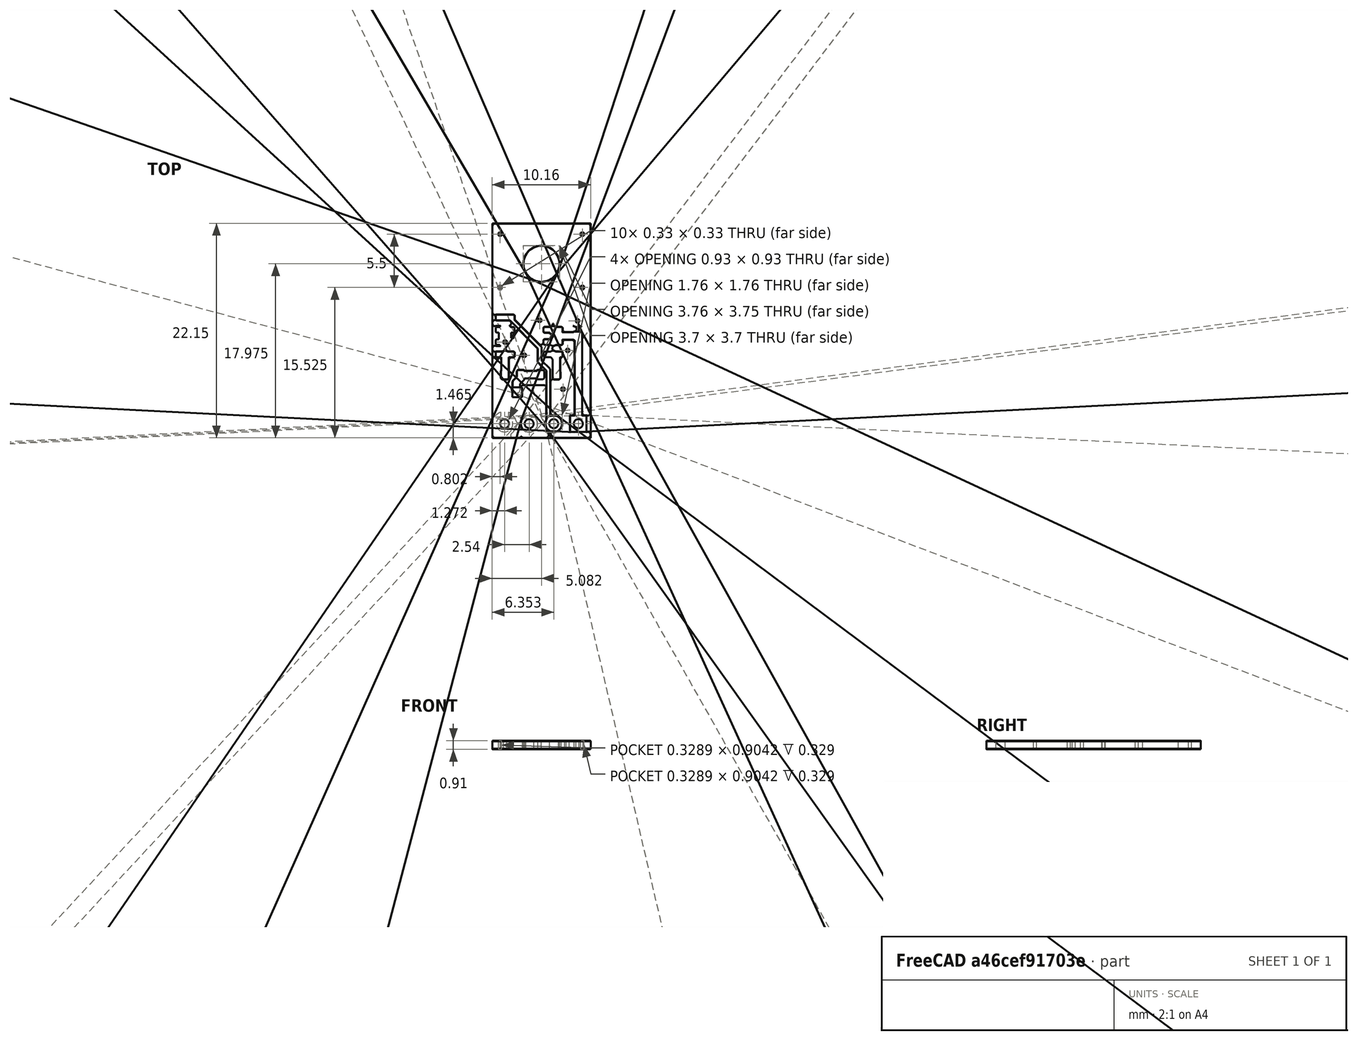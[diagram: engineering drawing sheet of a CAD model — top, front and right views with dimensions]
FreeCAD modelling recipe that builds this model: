
FCSTD DOCUMENT  (FreeCAD 0.21R29506 (Git))
Label: heat_sim
License: All rights reserved
LicenseURL: http://en.wikipedia.org/wiki/All_rights_reserved
objects: Path::FeatureArea×35, Part::Feature×33, Part::Extrusion×5, Part::Compound×4, Part::MultiFuse×2, App::MaterialObjectPython×2, Fem::ConstraintTemperature×2, Part::Cut×1, Part::Box×1, Fem::FemMeshObjectPython×1, App::FeaturePython×1, App::TextDocument×1, Fem::FemPostPipeline×1, Fem::FemSolverObjectPython×1, Fem::FemAnalysis×1
note: 116 computed .brp shape members not serialized (recipe doc carries the construction recipe); baked Part::Feature solids carry a one-line shape summary decoded from their .brp

FEATURE [Part::Feature] holes_wire  label="holes_wire#F.Cu#0"
  shape: bbox 3.7 x 3.7 x 2e-07 mm, 0 faces, 0 solids (baked)
FEATURE [Part::Feature] pads_wire  label="pads_wire#F.Cu#0#"REF**""
  shape: bbox 3.7 x 3.7 x 2e-07 mm, 0 faces, 0 solids (baked)
FEATURE [Path::FeatureArea] pads_area  label="pads_area#F.Cu#0#"REF**""
  Accuracy = 0.0005
  Angle = 45
  AngleShift = 0
  CleanDistance = 0
  ClipFill = 0
  ClipperScale = 10000000
  Coplanar = 0
  Deflection = 0.01
  EndType = 0
  Explode = false
  ExtraPass = 0
  Fill = 1
  FitArcs = false
  FromCenter = false
  JoinType = 0
  LastStepover = 0
  MaxArcPoints = 100
  MinArcPoints = 4
  MiterLimit = 2
  OpenMode = 0
  Operation = 0
  Outline = false
  Placement = pos=(4.90232,-4.455,0) rot=(0,0,1;0rad)
  PocketExtraOffset = 0
  PocketLastStepover = 0
  PocketMode = 0
  PocketStepover = 0
  Project = false
  Reorient = false
  RoundPrecision = 0
  SectionCount = 0
  SectionMode = 2
  SectionOffset = 0
  SectionTolerance = 1e-06
  Shift = 0
  Simplify = false
  Sources = -> [pads_wire]
  Stepdown = 1
  Stepover = 0
  SubjectFill = 0
  Thicken = false
  Tolerance = 1e-07
  ToolRadius = 1
  Unit = 1
FEATURE [Part::Feature] pads_wire001  label="pads_wire001#F.Cu#1#"Q1""
  shape: bbox 0.65 x 0.65 x 2e-07 mm, 0 faces, 0 solids (baked)
FEATURE [Path::FeatureArea] pads_area001  label="pads_area001#F.Cu#1#"Q1""
  Accuracy = 0.0005
  Angle = 45
  AngleShift = 0
  CleanDistance = 0
  ClipFill = 0
  ClipperScale = 10000000
  Coplanar = 0
  Deflection = 0.01
  EndType = 0
  Explode = false
  ExtraPass = 0
  Fill = 1
  FitArcs = false
  FromCenter = false
  JoinType = 0
  LastStepover = 0
  MaxArcPoints = 100
  MinArcPoints = 4
  MiterLimit = 2
  OpenMode = 0
  Operation = 0
  Outline = false
  Placement = pos=(2.34232,-18.285,0) rot=(0,0,1;1.5708rad)
  PocketExtraOffset = 0
  PocketLastStepover = 0
  PocketMode = 0
  PocketStepover = 0
  Project = false
  Reorient = false
  RoundPrecision = 0
  SectionCount = 0
  SectionMode = 2
  SectionOffset = 0
  SectionTolerance = 1e-06
  Shift = 0
  Simplify = false
  Sources = -> [pads_wire001]
  Stepdown = 1
  Stepover = 0
  SubjectFill = 0
  Thicken = false
  Tolerance = 1e-07
  ToolRadius = 1
  Unit = 1
FEATURE [Part::Feature] pads_wire002  label="pads_wire002#F.Cu#2#"C1""
  shape: bbox 2.45 x 0.95 x 2e-07 mm, 0 faces, 0 solids (baked)
FEATURE [Path::FeatureArea] pads_area002  label="pads_area002#F.Cu#2#"C1""
  Accuracy = 0.0005
  Angle = 45
  AngleShift = 0
  CleanDistance = 0
  ClipFill = 0
  ClipperScale = 10000000
  Coplanar = 0
  Deflection = 0.01
  EndType = 0
  Explode = false
  ExtraPass = 0
  Fill = 1
  FitArcs = false
  FromCenter = false
  JoinType = 0
  LastStepover = 0
  MaxArcPoints = 100
  MinArcPoints = 4
  MiterLimit = 2
  OpenMode = 0
  Operation = 0
  Outline = false
  Placement = pos=(8.62232,-11.13,0) rot=(0,0,1;1.5708rad)
  PocketExtraOffset = 0
  PocketLastStepover = 0
  PocketMode = 0
  PocketStepover = 0
  Project = false
  Reorient = false
  RoundPrecision = 0
  SectionCount = 0
  SectionMode = 2
  SectionOffset = 0
  SectionTolerance = 1e-06
  Shift = 0
  Simplify = false
  Sources = -> [pads_wire002]
  Stepdown = 1
  Stepover = 0
  SubjectFill = 0
  Thicken = false
  Tolerance = 1e-07
  ToolRadius = 1
  Unit = 1
FEATURE [Part::Feature] pads_wire003  label="pads_wire003#F.Cu#3#"R2""
  shape: bbox 2.45 x 0.95 x 2e-07 mm, 0 faces, 0 solids (baked)
FEATURE [Path::FeatureArea] pads_area003  label="pads_area003#F.Cu#3#"R2""
  Accuracy = 0.0005
  Angle = 45
  AngleShift = 0
  CleanDistance = 0
  ClipFill = 0
  ClipperScale = 10000000
  Coplanar = 0
  Deflection = 0.01
  EndType = 0
  Explode = false
  ExtraPass = 0
  Fill = 1
  FitArcs = false
  FromCenter = false
  JoinType = 0
  LastStepover = 0
  MaxArcPoints = 100
  MinArcPoints = 4
  MiterLimit = 2
  OpenMode = 0
  Operation = 0
  Outline = false
  Placement = pos=(5.62232,-15.905,0) rot=(0,0,1;3.14159rad)
  PocketExtraOffset = 0
  PocketLastStepover = 0
  PocketMode = 0
  PocketStepover = 0
  Project = false
  Reorient = false
  RoundPrecision = 0
  SectionCount = 0
  SectionMode = 2
  SectionOffset = 0
  SectionTolerance = 1e-06
  Shift = 0
  Simplify = false
  Sources = -> [pads_wire003]
  Stepdown = 1
  Stepover = 0
  SubjectFill = 0
  Thicken = false
  Tolerance = 1e-07
  ToolRadius = 1
  Unit = 1
FEATURE [Part::Feature] pads_wire004  label="pads_wire004#F.Cu#4#"R1""
  shape: bbox 2.45 x 0.95 x 2e-07 mm, 0 faces, 0 solids (baked)
FEATURE [Path::FeatureArea] pads_area004  label="pads_area004#F.Cu#4#"R1""
  Accuracy = 0.0005
  Angle = 45
  AngleShift = 0
  CleanDistance = 0
  ClipFill = 0
  ClipperScale = 10000000
  Coplanar = 0
  Deflection = 0.01
  EndType = 0
  Explode = false
  ExtraPass = 0
  Fill = 1
  FitArcs = false
  FromCenter = false
  JoinType = 0
  LastStepover = 0
  MaxArcPoints = 100
  MinArcPoints = 4
  MiterLimit = 2
  OpenMode = 0
  Operation = 0
  Outline = false
  Placement = pos=(1.94732,-15.905,0) rot=(0,0,1;0rad)
  PocketExtraOffset = 0
  PocketLastStepover = 0
  PocketMode = 0
  PocketStepover = 0
  Project = false
  Reorient = false
  RoundPrecision = 0
  SectionCount = 0
  SectionMode = 2
  SectionOffset = 0
  SectionTolerance = 1e-06
  Shift = 0
  Simplify = false
  Sources = -> [pads_wire004]
  Stepdown = 1
  Stepover = 0
  SubjectFill = 0
  Thicken = false
  Tolerance = 1e-07
  ToolRadius = 1
  Unit = 1
FEATURE [Part::Feature] pads_wire005  label="pads_wire005#F.Cu#5#"U1""
  shape: bbox 6.9 x 4.41 x 2e-07 mm, 0 faces, 0 solids (baked)
FEATURE [Path::FeatureArea] pads_area005  label="pads_area005#F.Cu#5#"U1""
  Accuracy = 0.0005
  Angle = 45
  AngleShift = 0
  CleanDistance = 0
  ClipFill = 0
  ClipperScale = 10000000
  Coplanar = 0
  Deflection = 0.01
  EndType = 0
  Explode = false
  ExtraPass = 0
  Fill = 1
  FitArcs = false
  FromCenter = false
  JoinType = 0
  LastStepover = 0
  MaxArcPoints = 100
  MinArcPoints = 4
  MiterLimit = 2
  OpenMode = 0
  Operation = 0
  Outline = false
  Placement = pos=(3.62232,-11.905,0) rot=(0,0,1;0rad)
  PocketExtraOffset = 0
  PocketLastStepover = 0
  PocketMode = 0
  PocketStepover = 0
  Project = false
  Reorient = false
  RoundPrecision = 0
  SectionCount = 0
  SectionMode = 2
  SectionOffset = 0
  SectionTolerance = 1e-06
  Shift = 0
  Simplify = false
  Sources = -> [pads_wire005]
  Stepdown = 1
  Stepover = 0
  SubjectFill = 0
  Thicken = false
  Tolerance = 1e-07
  ToolRadius = 1
  Unit = 1
FEATURE [Part::Feature] pads_wire006  label="pads_wire006#F.Cu#6#"J1""
  shape: bbox 1.7 x 9.32 x 2e-07 mm, 0 faces, 0 solids (baked)
FEATURE [Path::FeatureArea] pads_area006  label="pads_area006#F.Cu#6#"J1""
  Accuracy = 0.0005
  Angle = 45
  AngleShift = 0
  CleanDistance = 0
  ClipFill = 0
  ClipperScale = 10000000
  Coplanar = 0
  Deflection = 0.01
  EndType = 0
  Explode = false
  ExtraPass = 0
  Fill = 1
  FitArcs = false
  FromCenter = false
  JoinType = 0
  LastStepover = 0
  MaxArcPoints = 100
  MinArcPoints = 4
  MiterLimit = 2
  OpenMode = 0
  Operation = 0
  Outline = false
  Placement = pos=(8.71232,-20.965,0) rot=(0,0,-1;1.5708rad)
  PocketExtraOffset = 0
  PocketLastStepover = 0
  PocketMode = 0
  PocketStepover = 0
  Project = false
  Reorient = false
  RoundPrecision = 0
  SectionCount = 0
  SectionMode = 2
  SectionOffset = 0
  SectionTolerance = 1e-06
  Shift = 0
  Simplify = false
  Sources = -> [pads_wire006]
  Stepdown = 1
  Stepover = 0
  SubjectFill = 0
  Thicken = false
  Tolerance = 1e-07
  ToolRadius = 1
  Unit = 1
FEATURE [Part::Feature] vias_wire  label="vias_wire#F.Cu"
  shape: bbox 9.3 x 16.8 x 2e-07 mm, 0 faces, 0 solids (baked)
FEATURE [Path::FeatureArea] vias_area  label="vias_area#F.Cu"
  Accuracy = 0.0005
  Angle = 45
  AngleShift = 0
  CleanDistance = 0
  ClipFill = 0
  ClipperScale = 10000000
  Coplanar = 0
  Deflection = 0.01
  EndType = 0
  Explode = false
  ExtraPass = 0
  Fill = 1
  FitArcs = false
  FromCenter = false
  JoinType = 0
  LastStepover = 0
  MaxArcPoints = 100
  MinArcPoints = 4
  MiterLimit = 2
  OpenMode = 0
  Operation = 0
  Outline = false
  PocketExtraOffset = 0
  PocketLastStepover = 0
  PocketMode = 0
  PocketStepover = 0
  Project = false
  Reorient = false
  RoundPrecision = 0
  SectionCount = 0
  SectionMode = 2
  SectionOffset = 0
  SectionTolerance = 1e-06
  Shift = 0
  Simplify = false
  Sources = -> [vias_wire]
  Stepdown = 1
  Stepover = 0
  SubjectFill = 0
  Thicken = false
  Tolerance = 1e-07
  ToolRadius = 1
  Unit = 1
FEATURE [Part::Compound] pads_combo  label="pads_combo#F.Cu"
  Links = -> [pads_area,pads_area001,pads_area002,pads_area003,pads_area004,pads_area005,pads_area006,vias_area]
FEATURE [Path::FeatureArea] pads_area007  label="pads_area007#F.Cu"
  Accuracy = 0.0005
  Angle = 45
  AngleShift = 0
  CleanDistance = 0
  ClipFill = 0
  ClipperScale = 10000000
  Coplanar = 0
  Deflection = 0.01
  EndType = 0
  Explode = false
  ExtraPass = 0
  Fill = 2
  FitArcs = true
  FromCenter = false
  JoinType = 0
  LastStepover = 0
  MaxArcPoints = 100
  MinArcPoints = 4
  MiterLimit = 2
  OpenMode = 0
  Operation = 1
  Outline = false
  PocketExtraOffset = 0
  PocketLastStepover = 0
  PocketMode = 0
  PocketStepover = 0
  Project = false
  Reorient = false
  RoundPrecision = 0
  SectionCount = 0
  SectionMode = 2
  SectionOffset = 0
  SectionTolerance = 1e-06
  Shift = 0
  Simplify = false
  Sources = -> [pads_combo,holes_wire]
  Stepdown = 1
  Stepover = 0
  SubjectFill = 0
  Thicken = false
  Tolerance = 1e-07
  ToolRadius = 1
  Unit = 1
FEATURE [Part::Feature] track_wire  label="track_wire#F.Cu#0.762"
  shape: bbox 7.59 x 9.695 x 2e-07 mm, 0 faces, 0 solids (baked)
FEATURE [Path::FeatureArea] track_area  label="track_area#F.Cu#0.762"
  Accuracy = 0.0005
  Angle = 45
  AngleShift = 0
  CleanDistance = 0
  ClipFill = 0
  ClipperScale = 10000000
  Coplanar = 0
  Deflection = 0.01
  EndType = 0
  Explode = false
  ExtraPass = 0
  Fill = 1
  FitArcs = true
  FromCenter = false
  JoinType = 0
  LastStepover = 0
  MaxArcPoints = 100
  MinArcPoints = 4
  MiterLimit = 2
  Offset = 0.381
  OpenMode = 0
  Operation = 0
  Outline = false
  PocketExtraOffset = 0
  PocketLastStepover = 0
  PocketMode = 0
  PocketStepover = 0
  Project = false
  Reorient = false
  RoundPrecision = 0
  SectionCount = 0
  SectionMode = 2
  SectionOffset = 0
  SectionTolerance = 1e-06
  Shift = 0
  Simplify = false
  Sources = -> [track_wire]
  Stepdown = 1
  Stepover = 0
  SubjectFill = 0
  Thicken = false
  Tolerance = 1e-07
  ToolRadius = 1
  Unit = 1
FEATURE [Part::Feature] track_wire001  label="track_wire001#F.Cu#0.254"
  shape: bbox 2.54 x 3.355 x 2e-07 mm, 0 faces, 0 solids (baked)
FEATURE [Path::FeatureArea] track_area001  label="track_area001#F.Cu#0.254"
  Accuracy = 0.0005
  Angle = 45
  AngleShift = 0
  CleanDistance = 0
  ClipFill = 0
  ClipperScale = 10000000
  Coplanar = 0
  Deflection = 0.01
  EndType = 0
  Explode = false
  ExtraPass = 0
  Fill = 1
  FitArcs = true
  FromCenter = false
  JoinType = 0
  LastStepover = 0
  MaxArcPoints = 100
  MinArcPoints = 4
  MiterLimit = 2
  Offset = 0.127
  OpenMode = 0
  Operation = 0
  Outline = false
  PocketExtraOffset = 0
  PocketLastStepover = 0
  PocketMode = 0
  PocketStepover = 0
  Project = false
  Reorient = false
  RoundPrecision = 0
  SectionCount = 0
  SectionMode = 2
  SectionOffset = 0
  SectionTolerance = 1e-06
  Shift = 0
  Simplify = false
  Sources = -> [track_wire001]
  Stepdown = 1
  Stepover = 0
  SubjectFill = 0
  Thicken = false
  Tolerance = 1e-07
  ToolRadius = 1
  Unit = 1
FEATURE [Part::Feature] track_wire002  label="track_wire002#F.Cu#1.27"
  shape: bbox 7.475 x 2.54 x 2e-07 mm, 0 faces, 0 solids (baked)
FEATURE [Path::FeatureArea] track_area002  label="track_area002#F.Cu#1.27"
  Accuracy = 0.0005
  Angle = 45
  AngleShift = 0
  CleanDistance = 0
  ClipFill = 0
  ClipperScale = 10000000
  Coplanar = 0
  Deflection = 0.01
  EndType = 0
  Explode = false
  ExtraPass = 0
  Fill = 1
  FitArcs = true
  FromCenter = false
  JoinType = 0
  LastStepover = 0
  MaxArcPoints = 100
  MinArcPoints = 4
  MiterLimit = 2
  Offset = 0.635
  OpenMode = 0
  Operation = 0
  Outline = false
  PocketExtraOffset = 0
  PocketLastStepover = 0
  PocketMode = 0
  PocketStepover = 0
  Project = false
  Reorient = false
  RoundPrecision = 0
  SectionCount = 0
  SectionMode = 2
  SectionOffset = 0
  SectionTolerance = 1e-06
  Shift = 0
  Simplify = false
  Sources = -> [track_wire002]
  Stepdown = 1
  Stepover = 0
  SubjectFill = 0
  Thicken = false
  Tolerance = 1e-07
  ToolRadius = 1
  Unit = 1
FEATURE [Part::Feature] track_wire003  label="track_wire003#F.Cu#0.381"
  shape: bbox 5.025 x 10.97 x 2e-07 mm, 0 faces, 0 solids (baked)
FEATURE [Path::FeatureArea] track_area003  label="track_area003#F.Cu#0.381"
  Accuracy = 0.0005
  Angle = 45
  AngleShift = 0
  CleanDistance = 0
  ClipFill = 0
  ClipperScale = 10000000
  Coplanar = 0
  Deflection = 0.01
  EndType = 0
  Explode = false
  ExtraPass = 0
  Fill = 1
  FitArcs = true
  FromCenter = false
  JoinType = 0
  LastStepover = 0
  MaxArcPoints = 100
  MinArcPoints = 4
  MiterLimit = 2
  Offset = 0.1905
  OpenMode = 0
  Operation = 0
  Outline = false
  PocketExtraOffset = 0
  PocketLastStepover = 0
  PocketMode = 0
  PocketStepover = 0
  Project = false
  Reorient = false
  RoundPrecision = 0
  SectionCount = 0
  SectionMode = 2
  SectionOffset = 0
  SectionTolerance = 1e-06
  Shift = 0
  Simplify = false
  Sources = -> [track_wire003]
  Stepdown = 1
  Stepover = 0
  SubjectFill = 0
  Thicken = false
  Tolerance = 1e-07
  ToolRadius = 1
  Unit = 1
FEATURE [Part::Compound] tracks_combo  label="tracks_combo#F.Cu"
  Links = -> [track_area,track_area001,track_area002,track_area003]
FEATURE [Path::FeatureArea] tracks_area  label="tracks_area#F.Cu"
  Accuracy = 0.0005
  Angle = 45
  AngleShift = 0
  CleanDistance = 0
  ClipFill = 0
  ClipperScale = 10000000
  Coplanar = 0
  Deflection = 0.01
  EndType = 0
  Explode = false
  ExtraPass = 0
  Fill = 2
  FitArcs = true
  FromCenter = false
  JoinType = 0
  LastStepover = 0
  MaxArcPoints = 100
  MinArcPoints = 4
  MiterLimit = 2
  OpenMode = 0
  Operation = 1
  Outline = false
  PocketExtraOffset = 0
  PocketLastStepover = 0
  PocketMode = 0
  PocketStepover = 0
  Project = false
  Reorient = false
  RoundPrecision = 0
  SectionCount = 0
  SectionMode = 2
  SectionOffset = 0
  SectionTolerance = 1e-06
  Shift = 0
  Simplify = false
  Sources = -> [tracks_combo,holes_wire]
  Stepdown = 1
  Stepover = 0
  SubjectFill = 0
  Thicken = false
  Tolerance = 1e-07
  ToolRadius = 1
  Unit = 1
FEATURE [Part::Feature] zone_wire  label="zone_wire#F.Cu#"GND""
  shape: bbox 3.907 x 9.843 x 2e-07 mm, 0 faces, 0 solids (baked)
FEATURE [Path::FeatureArea] zone_area  label="zone_area#F.Cu#"GND""
  Accuracy = 0.0005
  Angle = 45
  AngleShift = 0
  CleanDistance = 0
  ClipFill = 0
  ClipperScale = 10000000
  Coplanar = 0
  Deflection = 0.01
  EndType = 0
  Explode = false
  ExtraPass = 0
  Fill = 1
  FitArcs = false
  FromCenter = false
  JoinType = 0
  LastStepover = 0
  MaxArcPoints = 100
  MinArcPoints = 4
  MiterLimit = 2
  Offset = 0.127
  OpenMode = 0
  Operation = 0
  Outline = false
  PocketExtraOffset = 0
  PocketLastStepover = 0
  PocketMode = 0
  PocketStepover = 0
  Project = false
  Reorient = false
  RoundPrecision = 0
  SectionCount = 0
  SectionMode = 2
  SectionOffset = 0
  SectionTolerance = 1e-06
  Shift = 0
  Simplify = false
  Sources = -> [zone_wire]
  Stepdown = 1
  Stepover = 0
  SubjectFill = 0
  Thicken = false
  Tolerance = 1e-07
  ToolRadius = 1
  Unit = 1
FEATURE [Part::Feature] zone_outline_wire  label="zone_outline_wire#F.Cu#"GND""
  shape: bbox 9.854 x 19.57 x 2e-07 mm, 0 faces, 0 solids (baked)
FEATURE [Part::Feature] zone_hole_wire  label="zone_hole_wire#F.Cu#"GND""
  shape: bbox 6.427 x 7.522 x 2e-07 mm, 0 faces, 0 solids (baked)
FEATURE [Path::FeatureArea] zone_area001  label="zone_area001#F.Cu#"GND""
  Accuracy = 0.0005
  Angle = 45
  AngleShift = 0
  CleanDistance = 0
  ClipFill = 0
  ClipperScale = 10000000
  Coplanar = 0
  Deflection = 0.01
  EndType = 0
  Explode = false
  ExtraPass = 0
  Fill = 1
  FitArcs = false
  FromCenter = false
  JoinType = 0
  LastStepover = 0
  MaxArcPoints = 100
  MinArcPoints = 4
  MiterLimit = 2
  Offset = 0.127
  OpenMode = 0
  Operation = 1
  Outline = false
  PocketExtraOffset = 0
  PocketLastStepover = 0
  PocketMode = 0
  PocketStepover = 0
  Project = false
  Reorient = false
  RoundPrecision = 0
  SectionCount = 0
  SectionMode = 2
  SectionOffset = 0
  SectionTolerance = 1e-06
  Shift = 0
  Simplify = false
  Sources = -> [zone_outline_wire,zone_hole_wire]
  Stepdown = 1
  Stepover = 0
  SubjectFill = 0
  Thicken = false
  Tolerance = 1e-07
  ToolRadius = 1
  Unit = 1
FEATURE [Part::Feature] zone_wire001  label="zone_wire001#F.Cu#"GND""
  shape: bbox 4.837 x 5.488 x 2e-07 mm, 0 faces, 0 solids (baked)
FEATURE [Path::FeatureArea] zone_area002  label="zone_area002#F.Cu#"GND""
  Accuracy = 0.0005
  Angle = 45
  AngleShift = 0
  CleanDistance = 0
  ClipFill = 0
  ClipperScale = 10000000
  Coplanar = 0
  Deflection = 0.01
  EndType = 0
  Explode = false
  ExtraPass = 0
  Fill = 1
  FitArcs = false
  FromCenter = false
  JoinType = 0
  LastStepover = 0
  MaxArcPoints = 100
  MinArcPoints = 4
  MiterLimit = 2
  Offset = 0.127
  OpenMode = 0
  Operation = 0
  Outline = false
  PocketExtraOffset = 0
  PocketLastStepover = 0
  PocketMode = 0
  PocketStepover = 0
  Project = false
  Reorient = false
  RoundPrecision = 0
  SectionCount = 0
  SectionMode = 2
  SectionOffset = 0
  SectionTolerance = 1e-06
  Shift = 0
  Simplify = false
  Sources = -> [zone_wire001]
  Stepdown = 1
  Stepover = 0
  SubjectFill = 0
  Thicken = false
  Tolerance = 1e-07
  ToolRadius = 1
  Unit = 1
FEATURE [Part::Feature] zone_wire002  label="zone_wire002#F.Cu#"GND""
  shape: bbox 1.001 x 0.3659 x 2e-07 mm, 0 faces, 0 solids (baked)
FEATURE [Path::FeatureArea] zone_area003  label="zone_area003#F.Cu#"GND""
  Accuracy = 0.0005
  Angle = 45
  AngleShift = 0
  CleanDistance = 0
  ClipFill = 0
  ClipperScale = 10000000
  Coplanar = 0
  Deflection = 0.01
  EndType = 0
  Explode = false
  ExtraPass = 0
  Fill = 1
  FitArcs = false
  FromCenter = false
  JoinType = 0
  LastStepover = 0
  MaxArcPoints = 100
  MinArcPoints = 4
  MiterLimit = 2
  Offset = 0.127
  OpenMode = 0
  Operation = 0
  Outline = false
  PocketExtraOffset = 0
  PocketLastStepover = 0
  PocketMode = 0
  PocketStepover = 0
  Project = false
  Reorient = false
  RoundPrecision = 0
  SectionCount = 0
  SectionMode = 2
  SectionOffset = 0
  SectionTolerance = 1e-06
  Shift = 0
  Simplify = false
  Sources = -> [zone_wire002]
  Stepdown = 1
  Stepover = 0
  SubjectFill = 0
  Thicken = false
  Tolerance = 1e-07
  ToolRadius = 1
  Unit = 1
FEATURE [Part::Feature] zone_wire003  label="zone_wire003#F.Cu#"GND""
  shape: bbox 1.69 x 1.173 x 2e-07 mm, 0 faces, 0 solids (baked)
FEATURE [Path::FeatureArea] zone_area004  label="zone_area004#F.Cu#"GND""
  Accuracy = 0.0005
  Angle = 45
  AngleShift = 0
  CleanDistance = 0
  ClipFill = 0
  ClipperScale = 10000000
  Coplanar = 0
  Deflection = 0.01
  EndType = 0
  Explode = false
  ExtraPass = 0
  Fill = 1
  FitArcs = false
  FromCenter = false
  JoinType = 0
  LastStepover = 0
  MaxArcPoints = 100
  MinArcPoints = 4
  MiterLimit = 2
  Offset = 0.127
  OpenMode = 0
  Operation = 0
  Outline = false
  PocketExtraOffset = 0
  PocketLastStepover = 0
  PocketMode = 0
  PocketStepover = 0
  Project = false
  Reorient = false
  RoundPrecision = 0
  SectionCount = 0
  SectionMode = 2
  SectionOffset = 0
  SectionTolerance = 1e-06
  Shift = 0
  Simplify = false
  Sources = -> [zone_wire003]
  Stepdown = 1
  Stepover = 0
  SubjectFill = 0
  Thicken = false
  Tolerance = 1e-07
  ToolRadius = 1
  Unit = 1
FEATURE [Part::Feature] zone_outline_wire001  label="zone_outline_wire001#F.Cu#"/drain""
  shape: bbox 2.6 x 5.177 x 2e-07 mm, 0 faces, 0 solids (baked)
FEATURE [Part::Feature] zone_hole_wire001  label="zone_hole_wire001#F.Cu#"/drain""
  shape: bbox 0.5536 x 1.622 x 2e-07 mm, 0 faces, 0 solids (baked)
FEATURE [Path::FeatureArea] zone_area005  label="zone_area005#F.Cu#"/drain""
  Accuracy = 0.0005
  Angle = 45
  AngleShift = 0
  CleanDistance = 0
  ClipFill = 0
  ClipperScale = 10000000
  Coplanar = 0
  Deflection = 0.01
  EndType = 0
  Explode = false
  ExtraPass = 0
  Fill = 1
  FitArcs = false
  FromCenter = false
  JoinType = 0
  LastStepover = 0
  MaxArcPoints = 100
  MinArcPoints = 4
  MiterLimit = 2
  Offset = 0.127
  OpenMode = 0
  Operation = 1
  Outline = false
  PocketExtraOffset = 0
  PocketLastStepover = 0
  PocketMode = 0
  PocketStepover = 0
  Project = false
  Reorient = false
  RoundPrecision = 0
  SectionCount = 0
  SectionMode = 2
  SectionOffset = 0
  SectionTolerance = 1e-06
  Shift = 0
  Simplify = false
  Sources = -> [zone_outline_wire001,zone_hole_wire001]
  Stepdown = 1
  Stepover = 0
  SubjectFill = 0
  Thicken = false
  Tolerance = 1e-07
  ToolRadius = 1
  Unit = 1
FEATURE [Part::Feature] zone_outline_wire002  label="zone_outline_wire002#F.Cu#"GND""
  shape: bbox 2.747 x 5.377 x 2e-07 mm, 0 faces, 0 solids (baked)
FEATURE [Part::Feature] zone_hole_wire002  label="zone_hole_wire002#F.Cu#"GND""
  shape: bbox 1.615 x 1.623 x 2e-07 mm, 0 faces, 0 solids (baked)
FEATURE [Path::FeatureArea] zone_area006  label="zone_area006#F.Cu#"GND""
  Accuracy = 0.0005
  Angle = 45
  AngleShift = 0
  CleanDistance = 0
  ClipFill = 0
  ClipperScale = 10000000
  Coplanar = 0
  Deflection = 0.01
  EndType = 0
  Explode = false
  ExtraPass = 0
  Fill = 1
  FitArcs = false
  FromCenter = false
  JoinType = 0
  LastStepover = 0
  MaxArcPoints = 100
  MinArcPoints = 4
  MiterLimit = 2
  Offset = 0.127
  OpenMode = 0
  Operation = 1
  Outline = false
  PocketExtraOffset = 0
  PocketLastStepover = 0
  PocketMode = 0
  PocketStepover = 0
  Project = false
  Reorient = false
  RoundPrecision = 0
  SectionCount = 0
  SectionMode = 2
  SectionOffset = 0
  SectionTolerance = 1e-06
  Shift = 0
  Simplify = false
  Sources = -> [zone_outline_wire002,zone_hole_wire002]
  Stepdown = 1
  Stepover = 0
  SubjectFill = 0
  Thicken = false
  Tolerance = 1e-07
  ToolRadius = 1
  Unit = 1
FEATURE [Part::Compound] zones_combo  label="zones_combo#F.Cu"
  Links = -> [zone_area,zone_area001,zone_area002,zone_area003,zone_area004,zone_area005,zone_area006]
FEATURE [Path::FeatureArea] zones_area  label="zones_area#F.Cu"
  Accuracy = 0.0005
  Angle = 45
  AngleShift = 0
  CleanDistance = 0
  ClipFill = 0
  ClipperScale = 10000000
  Coplanar = 0
  Deflection = 0.01
  EndType = 0
  Explode = false
  ExtraPass = 0
  Fill = 2
  FitArcs = false
  FromCenter = false
  JoinType = 0
  LastStepover = 0
  MaxArcPoints = 100
  MinArcPoints = 4
  MiterLimit = 2
  OpenMode = 0
  Operation = 1
  Outline = false
  PocketExtraOffset = 0
  PocketLastStepover = 0
  PocketMode = 0
  PocketStepover = 0
  Project = false
  Reorient = false
  RoundPrecision = 0
  SectionCount = 0
  SectionMode = 2
  SectionOffset = 0
  SectionTolerance = 1e-06
  Shift = 0
  Simplify = false
  Sources = -> [zones_combo,holes_wire]
  Stepdown = 1
  Stepover = 0
  SubjectFill = 0
  Thicken = false
  Tolerance = 1e-07
  ToolRadius = 1
  Unit = 1
FEATURE [Path::FeatureArea] copper_area  label="copper_area#F.Cu"
  Accuracy = 0.0005
  Angle = 45
  AngleShift = 0
  CleanDistance = 0
  ClipFill = 0
  ClipperScale = 10000000
  Coplanar = 0
  Deflection = 0.01
  EndType = 0
  Explode = false
  ExtraPass = 0
  Fill = 2
  FitArcs = true
  FromCenter = false
  JoinType = 0
  LastStepover = 0
  MaxArcPoints = 100
  MinArcPoints = 4
  MiterLimit = 2
  OpenMode = 0
  Operation = 0
  Outline = false
  PocketExtraOffset = 0
  PocketLastStepover = 0
  PocketMode = 0
  PocketStepover = 0
  Project = false
  Reorient = false
  RoundPrecision = 0
  SectionCount = 0
  SectionMode = 2
  SectionOffset = 0
  SectionTolerance = 1e-06
  Shift = 0
  Simplify = false
  Sources = -> [pads_area007,tracks_area,zones_area]
  Stepdown = 1
  Stepover = 0
  SubjectFill = 0
  Thicken = false
  Tolerance = 1e-07
  ToolRadius = 1
  Unit = 1
FEATURE [Part::Extrusion] copper_solid  label="copper_solid#F.Cu"
  Base = -> copper_area
  Dir = (0,0,0.0711)
  DirMode = 0
  FaceMakerClass = Part::FaceMakerBullseye
  LengthFwd = 0
  LengthRev = 0
  Placement = pos=(0,0,0.762) rot=(0,0,1;0rad)
  Solid = false
  Symmetric = false
FEATURE [Part::Feature] pads_wire007  label="pads_wire007#B.Cu#0#"REF**""
  shape: bbox 3.7 x 3.7 x 2e-07 mm, 0 faces, 0 solids (baked)
FEATURE [Path::FeatureArea] pads_area008  label="pads_area008#B.Cu#0#"REF**""
  Accuracy = 0.0005
  Angle = 45
  AngleShift = 0
  CleanDistance = 0
  ClipFill = 0
  ClipperScale = 10000000
  Coplanar = 0
  Deflection = 0.01
  EndType = 0
  Explode = false
  ExtraPass = 0
  Fill = 1
  FitArcs = false
  FromCenter = false
  JoinType = 0
  LastStepover = 0
  MaxArcPoints = 100
  MinArcPoints = 4
  MiterLimit = 2
  OpenMode = 0
  Operation = 0
  Outline = false
  Placement = pos=(4.90232,-4.455,0) rot=(0,0,1;0rad)
  PocketExtraOffset = 0
  PocketLastStepover = 0
  PocketMode = 0
  PocketStepover = 0
  Project = false
  Reorient = false
  RoundPrecision = 0
  SectionCount = 0
  SectionMode = 2
  SectionOffset = 0
  SectionTolerance = 1e-06
  Shift = 0
  Simplify = false
  Sources = -> [pads_wire007]
  Stepdown = 1
  Stepover = 0
  SubjectFill = 0
  Thicken = false
  Tolerance = 1e-07
  ToolRadius = 1
  Unit = 1
FEATURE [Part::Feature] pads_wire008  label="pads_wire008#B.Cu#6#"J1""
  shape: bbox 1.7 x 9.32 x 2e-07 mm, 0 faces, 0 solids (baked)
FEATURE [Path::FeatureArea] pads_area009  label="pads_area009#B.Cu#6#"J1""
  Accuracy = 0.0005
  Angle = 45
  AngleShift = 0
  CleanDistance = 0
  ClipFill = 0
  ClipperScale = 10000000
  Coplanar = 0
  Deflection = 0.01
  EndType = 0
  Explode = false
  ExtraPass = 0
  Fill = 1
  FitArcs = false
  FromCenter = false
  JoinType = 0
  LastStepover = 0
  MaxArcPoints = 100
  MinArcPoints = 4
  MiterLimit = 2
  OpenMode = 0
  Operation = 0
  Outline = false
  Placement = pos=(8.71232,-20.965,0) rot=(0,0,-1;1.5708rad)
  PocketExtraOffset = 0
  PocketLastStepover = 0
  PocketMode = 0
  PocketStepover = 0
  Project = false
  Reorient = false
  RoundPrecision = 0
  SectionCount = 0
  SectionMode = 2
  SectionOffset = 0
  SectionTolerance = 1e-06
  Shift = 0
  Simplify = false
  Sources = -> [pads_wire008]
  Stepdown = 1
  Stepover = 0
  SubjectFill = 0
  Thicken = false
  Tolerance = 1e-07
  ToolRadius = 1
  Unit = 1
FEATURE [Part::Feature] vias_wire001  label="vias_wire001#B.Cu"
  shape: bbox 9.3 x 16.8 x 2e-07 mm, 0 faces, 0 solids (baked)
FEATURE [Path::FeatureArea] vias_area001  label="vias_area001#B.Cu"
  Accuracy = 0.0005
  Angle = 45
  AngleShift = 0
  CleanDistance = 0
  ClipFill = 0
  ClipperScale = 10000000
  Coplanar = 0
  Deflection = 0.01
  EndType = 0
  Explode = false
  ExtraPass = 0
  Fill = 1
  FitArcs = false
  FromCenter = false
  JoinType = 0
  LastStepover = 0
  MaxArcPoints = 100
  MinArcPoints = 4
  MiterLimit = 2
  OpenMode = 0
  Operation = 0
  Outline = false
  PocketExtraOffset = 0
  PocketLastStepover = 0
  PocketMode = 0
  PocketStepover = 0
  Project = false
  Reorient = false
  RoundPrecision = 0
  SectionCount = 0
  SectionMode = 2
  SectionOffset = 0
  SectionTolerance = 1e-06
  Shift = 0
  Simplify = false
  Sources = -> [vias_wire001]
  Stepdown = 1
  Stepover = 0
  SubjectFill = 0
  Thicken = false
  Tolerance = 1e-07
  ToolRadius = 1
  Unit = 1
FEATURE [Part::Compound] pads_combo001  label="pads_combo001#B.Cu"
  Links = -> [pads_area008,pads_area009,vias_area001]
FEATURE [Path::FeatureArea] pads_area010  label="pads_area010#B.Cu"
  Accuracy = 0.0005
  Angle = 45
  AngleShift = 0
  CleanDistance = 0
  ClipFill = 0
  ClipperScale = 10000000
  Coplanar = 0
  Deflection = 0.01
  EndType = 0
  Explode = false
  ExtraPass = 0
  Fill = 2
  FitArcs = true
  FromCenter = false
  JoinType = 0
  LastStepover = 0
  MaxArcPoints = 100
  MinArcPoints = 4
  MiterLimit = 2
  OpenMode = 0
  Operation = 1
  Outline = false
  PocketExtraOffset = 0
  PocketLastStepover = 0
  PocketMode = 0
  PocketStepover = 0
  Project = false
  Reorient = false
  RoundPrecision = 0
  SectionCount = 0
  SectionMode = 2
  SectionOffset = 0
  SectionTolerance = 1e-06
  Shift = 0
  Simplify = false
  Sources = -> [pads_combo001,holes_wire]
  Stepdown = 1
  Stepover = 0
  SubjectFill = 0
  Thicken = false
  Tolerance = 1e-07
  ToolRadius = 1
  Unit = 1
FEATURE [Part::Feature] track_wire004  label="track_wire004#B.Cu#1.27"
  shape: bbox 3.567 x 2.255 x 2e-07 mm, 0 faces, 0 solids (baked)
FEATURE [Path::FeatureArea] track_area004  label="track_area004#B.Cu#1.27"
  Accuracy = 0.0005
  Angle = 45
  AngleShift = 0
  CleanDistance = 0
  ClipFill = 0
  ClipperScale = 10000000
  Coplanar = 0
  Deflection = 0.01
  EndType = 0
  Explode = false
  ExtraPass = 0
  Fill = 1
  FitArcs = true
  FromCenter = false
  JoinType = 0
  LastStepover = 0
  MaxArcPoints = 100
  MinArcPoints = 4
  MiterLimit = 2
  Offset = 0.635
  OpenMode = 0
  Operation = 0
  Outline = false
  PocketExtraOffset = 0
  PocketLastStepover = 0
  PocketMode = 0
  PocketStepover = 0
  Project = false
  Reorient = false
  RoundPrecision = 0
  SectionCount = 0
  SectionMode = 2
  SectionOffset = 0
  SectionTolerance = 1e-06
  Shift = 0
  Simplify = false
  Sources = -> [track_wire004]
  Stepdown = 1
  Stepover = 0
  SubjectFill = 0
  Thicken = false
  Tolerance = 1e-07
  ToolRadius = 1
  Unit = 1
FEATURE [Path::FeatureArea] tracks_area001  label="tracks_area001#B.Cu"
  Accuracy = 0.0005
  Angle = 45
  AngleShift = 0
  CleanDistance = 0
  ClipFill = 0
  ClipperScale = 10000000
  Coplanar = 0
  Deflection = 0.01
  EndType = 0
  Explode = false
  ExtraPass = 0
  Fill = 2
  FitArcs = true
  FromCenter = false
  JoinType = 0
  LastStepover = 0
  MaxArcPoints = 100
  MinArcPoints = 4
  MiterLimit = 2
  OpenMode = 0
  Operation = 1
  Outline = false
  PocketExtraOffset = 0
  PocketLastStepover = 0
  PocketMode = 0
  PocketStepover = 0
  Project = false
  Reorient = false
  RoundPrecision = 0
  SectionCount = 0
  SectionMode = 2
  SectionOffset = 0
  SectionTolerance = 1e-06
  Shift = 0
  Simplify = false
  Sources = -> [track_area004,holes_wire]
  Stepdown = 1
  Stepover = 0
  SubjectFill = 0
  Thicken = false
  Tolerance = 1e-07
  ToolRadius = 1
  Unit = 1
FEATURE [Part::Feature] zone_outline_wire003  label="zone_outline_wire003#B.Cu#"GND""
  shape: bbox 9.854 x 21.85 x 2e-07 mm, 0 faces, 0 solids (baked)
FEATURE [Part::Feature] zone_hole_wire003  label="zone_hole_wire003#B.Cu#"GND""
  shape: bbox 4.286 x 19.52 x 2e-07 mm, 0 faces, 0 solids (baked)
FEATURE [Path::FeatureArea] zone_area007  label="zone_area007#B.Cu#"GND""
  Accuracy = 0.0005
  Angle = 45
  AngleShift = 0
  CleanDistance = 0
  ClipFill = 0
  ClipperScale = 10000000
  Coplanar = 0
  Deflection = 0.01
  EndType = 0
  Explode = false
  ExtraPass = 0
  Fill = 1
  FitArcs = false
  FromCenter = false
  JoinType = 0
  LastStepover = 0
  MaxArcPoints = 100
  MinArcPoints = 4
  MiterLimit = 2
  Offset = 0.127
  OpenMode = 0
  Operation = 1
  Outline = false
  PocketExtraOffset = 0
  PocketLastStepover = 0
  PocketMode = 0
  PocketStepover = 0
  Project = false
  Reorient = false
  RoundPrecision = 0
  SectionCount = 0
  SectionMode = 2
  SectionOffset = 0
  SectionTolerance = 1e-06
  Shift = 0
  Simplify = false
  Sources = -> [zone_outline_wire003,zone_hole_wire003]
  Stepdown = 1
  Stepover = 0
  SubjectFill = 0
  Thicken = false
  Tolerance = 1e-07
  ToolRadius = 1
  Unit = 1
FEATURE [Path::FeatureArea] zones_area001  label="zones_area001#B.Cu"
  Accuracy = 0.0005
  Angle = 45
  AngleShift = 0
  CleanDistance = 0
  ClipFill = 0
  ClipperScale = 10000000
  Coplanar = 0
  Deflection = 0.01
  EndType = 0
  Explode = false
  ExtraPass = 0
  Fill = 2
  FitArcs = false
  FromCenter = false
  JoinType = 0
  LastStepover = 0
  MaxArcPoints = 100
  MinArcPoints = 4
  MiterLimit = 2
  OpenMode = 0
  Operation = 1
  Outline = false
  PocketExtraOffset = 0
  PocketLastStepover = 0
  PocketMode = 0
  PocketStepover = 0
  Project = false
  Reorient = false
  RoundPrecision = 0
  SectionCount = 0
  SectionMode = 2
  SectionOffset = 0
  SectionTolerance = 1e-06
  Shift = 0
  Simplify = false
  Sources = -> [zone_area007,holes_wire]
  Stepdown = 1
  Stepover = 0
  SubjectFill = 0
  Thicken = false
  Tolerance = 1e-07
  ToolRadius = 1
  Unit = 1
FEATURE [Path::FeatureArea] copper_area001  label="copper_area001#B.Cu"
  Accuracy = 0.0005
  Angle = 45
  AngleShift = 0
  CleanDistance = 0
  ClipFill = 0
  ClipperScale = 10000000
  Coplanar = 0
  Deflection = 0.01
  EndType = 0
  Explode = false
  ExtraPass = 0
  Fill = 2
  FitArcs = true
  FromCenter = false
  JoinType = 0
  LastStepover = 0
  MaxArcPoints = 100
  MinArcPoints = 4
  MiterLimit = 2
  OpenMode = 0
  Operation = 0
  Outline = false
  PocketExtraOffset = 0
  PocketLastStepover = 0
  PocketMode = 0
  PocketStepover = 0
  Project = false
  Reorient = false
  RoundPrecision = 0
  SectionCount = 0
  SectionMode = 2
  SectionOffset = 0
  SectionTolerance = 1e-06
  Shift = 0
  Simplify = false
  Sources = -> [pads_area010,tracks_area001,zones_area001]
  Stepdown = 1
  Stepover = 0
  SubjectFill = 0
  Thicken = false
  Tolerance = 1e-07
  ToolRadius = 1
  Unit = 1
FEATURE [Part::Extrusion] copper_solid001  label="copper_solid001#B.Cu"
  Base = -> copper_area001
  Dir = (0,0,0.0711)
  DirMode = 0
  FaceMakerClass = Part::FaceMakerBullseye
  LengthFwd = 0
  LengthRev = 0
  Placement = pos=(0,0,-0.0711) rot=(0,0,1;0rad)
  Solid = false
  Symmetric = false
FEATURE [Part::Feature] holes_wire001  label="holes_wire001#F.Cu#0"
  shape: bbox 8.9 x 20.26 x 0.0711 mm, 0 faces, 0 solids (baked)
FEATURE [Path::FeatureArea] holes_area  label="holes_area#F.Cu#0"
  Accuracy = 0.0005
  Angle = 45
  AngleShift = 0
  CleanDistance = 0
  ClipFill = 0
  ClipperScale = 10000000
  Coplanar = 0
  Deflection = 0.01
  EndType = 0
  Explode = false
  ExtraPass = 0
  Fill = 1
  FitArcs = true
  FromCenter = false
  JoinType = 0
  LastStepover = 0
  MaxArcPoints = 100
  MinArcPoints = 4
  MiterLimit = 2
  OpenMode = 0
  Operation = 0
  Outline = false
  PocketExtraOffset = 0
  PocketLastStepover = 0
  PocketMode = 0
  PocketStepover = 0
  Project = false
  Reorient = false
  RoundPrecision = 0
  SectionCount = 0
  SectionMode = 2
  SectionOffset = 0
  SectionTolerance = 1e-06
  Shift = 0
  Simplify = false
  Sources = -> [holes_wire001]
  Stepdown = 1
  Stepover = 0
  SubjectFill = 0
  Thicken = false
  Tolerance = 1e-07
  ToolRadius = 1
  Unit = 1
FEATURE [Part::Extrusion] holes_solid  label="holes_solid#F.Cu#th"
  Base = -> holes_area
  Dir = (0,0,0.8331)
  DirMode = 0
  FaceMakerClass = Part::FaceMakerBullseye
  LengthFwd = 0
  LengthRev = 0
  Placement = pos=(0,0,-0.03555) rot=(0,0,1;0rad)
  Solid = false
  Symmetric = false
FEATURE [Part::MultiFuse] coppers_fuse  label="coppers_fuse#F.Cu"
  Shapes = -> [copper_solid,copper_solid001,holes_solid]
FEATURE [Part::Feature] holes_wire002  label="holes_wire002#F.Cu#0"
  shape: bbox 8.829 x 20.19 x 0.0711 mm, 0 faces, 0 solids (baked)
FEATURE [Path::FeatureArea] holes_area001  label="holes_area001#F.Cu#0"
  Accuracy = 0.0005
  Angle = 45
  AngleShift = 0
  CleanDistance = 0
  ClipFill = 0
  ClipperScale = 10000000
  Coplanar = 0
  Deflection = 0.01
  EndType = 0
  Explode = false
  ExtraPass = 0
  Fill = 1
  FitArcs = true
  FromCenter = false
  JoinType = 0
  LastStepover = 0
  MaxArcPoints = 100
  MinArcPoints = 4
  MiterLimit = 2
  OpenMode = 0
  Operation = 0
  Outline = false
  PocketExtraOffset = 0
  PocketLastStepover = 0
  PocketMode = 0
  PocketStepover = 0
  Project = false
  Reorient = false
  RoundPrecision = 0
  SectionCount = 0
  SectionMode = 2
  SectionOffset = 0
  SectionTolerance = 1e-06
  Shift = 0
  Simplify = false
  Sources = -> [holes_wire002]
  Stepdown = 1
  Stepover = 0
  SubjectFill = 0
  Thicken = false
  Tolerance = 1e-07
  ToolRadius = 1
  Unit = 1
FEATURE [Part::Extrusion] holes_solid001  label="holes_solid001#F.Cu#th"
  Base = -> holes_area001
  Dir = (0,0,1.0464)
  DirMode = 0
  FaceMakerClass = Part::FaceMakerBullseye
  LengthFwd = 0
  LengthRev = 0
  Placement = pos=(0,0,-0.0711) rot=(0,0,1;0rad)
  Solid = false
  Symmetric = false
FEATURE [Part::Cut] coppers_drilled  label="coppers_drilled#F.Cu"
  Base = -> coppers_fuse
  Tool = -> holes_solid001
FEATURE [Part::Feature] board_wire  label="board_wire#outline"
  shape: bbox 10.36 x 22.36 x 0.2 mm, 0 faces, 0 solids (baked)
FEATURE [Part::Feature] holes_wire003  label="holes_wire003#0"
  shape: bbox 8.9 x 20.26 x 0.0711 mm, 0 faces, 0 solids (baked)
FEATURE [Path::FeatureArea] board_area
  Accuracy = 0.0005
  Angle = 45
  AngleShift = 0
  CleanDistance = 0
  ClipFill = 0
  ClipperScale = 10000000
  Coplanar = 0
  Deflection = 0.01
  EndType = 0
  Explode = false
  ExtraPass = 0
  Fill = 1
  FitArcs = true
  FromCenter = false
  JoinType = 0
  LastStepover = 0
  MaxArcPoints = 100
  MinArcPoints = 4
  MiterLimit = 2
  OpenMode = 0
  Operation = 1
  Outline = false
  PocketExtraOffset = 0
  PocketLastStepover = 0
  PocketMode = 0
  PocketStepover = 0
  Project = false
  Reorient = false
  RoundPrecision = 0
  SectionCount = 0
  SectionMode = 2
  SectionOffset = 0
  SectionTolerance = 1e-06
  Shift = 0
  Simplify = false
  Sources = -> [board_wire,holes_wire003]
  Stepdown = 1
  Stepover = 0
  SubjectFill = 0
  Thicken = false
  Tolerance = 1e-07
  ToolRadius = 1
  Unit = 1
FEATURE [Part::Extrusion] board_solid
  Base = -> board_area
  Dir = (0,0,0.762)
  DirMode = 0
  FaceMakerClass = Part::FaceMakerBullseye
  LengthFwd = 0
  LengthRev = 0
  Solid = false
  Symmetric = false
FEATURE [Part::Box] Box  label="Cube"
  AttacherType = Attacher::AttachEngine3D
  Height = 0.01
  Length = 1
  Placement = pos=(1.9,-18.22,0.83) rot=(0,0,1;0rad)
  Width = 1
FEATURE [Part::MultiFuse] Fusion
  Shapes = -> [coppers_drilled,board_solid,Box]
FEATURE [Fem::FemMeshObjectPython] FEMMeshGmsh  # FEM object (typed FeaturePython)
  Algorithm2D = 0
  Algorithm3D = 0
  CharacteristicLengthMax = 0
  CharacteristicLengthMin = 0
  CoherenceMesh = true
  ElementDimension = 0
  ElementOrder = 1
  GeometryTolerance = 1e-06
  GroupsOfNodes = false
  HighOrderOptimize = 0
  MeshSizeFromCurvature = 12
  OptimizeNetgen = false
  OptimizeStd = true
  Part = -> Fusion
  RecombinationAlgorithm = 0
  Recombine3DAll = false
  RecombineAll = false
  SecondOrderLinear = false
FEATURE [App::FeaturePython] Heat  # WARN: FeaturePython — macro-defined, semantics opaque (R4)
  BiCGstablDegree = 0
  Bubbles = false
  LinearDirectMethod = 0
  LinearIterations = 500
  LinearIterativeMethod = 2
  LinearPreconditioning = 2
  LinearSolverType = 1
  LinearTolerance = 1e-08
  NonlinearIterations = 500
  NonlinearNewtonAfterIterations = 3
  NonlinearNewtonAfterTolerance = 0.001
  NonlinearTolerance = 1e-08
  Priority = 20
  RelaxationFactor = 1
  Stabilize = true
  SteadyStateTolerance = 1e-05
FEATURE [App::MaterialObjectPython] MaterialSolid  label="Copper"  # material (typed FeaturePython)
  Category = 0
  Material = AuthorAndLicense=no author; CardName=Copper; Color=Copper; Density=8930.000000000000 kg/m^3; ElectricalConductivity=58800000 mS/m; Name=Copper; PoissonRatio=0.343000000000000; ShearModulus=46.000000000000 GPa; SourceURL=https://www.matweb.com/search/datasheet.aspx?MatGUID=9aebe83845c04c1db5126fada6f76f7e&ckck=1; SpecificHeat=385.000000000 J/kg/K; ThermalConductivity=0395.000000000000 W/m/K; ThermalExpansionCoefficient=16.4000000000000 µm/m/K; YoungsModulus=130.000000000000 GPa
FEATURE [App::MaterialObjectPython] MaterialSolid001  label="FR4"  # material (typed FeaturePython)
  Category = 0
  Material = AuthorAndLicense=no author; CardName=FR4; Density=1850.000000000000 kg/m^3; Description=PCB; Dielectricstrength=20 MV/m; ElectricalConductivity=0.0000000000001 mS/m; KindOfMaterial=Composite; Name=FR4; PoissonRatio=0.12; RelativePermittivity=4.4; SpecificHeat=1150.000000000000 J/kg/K; ThermalConductivity=0.3430000000000 W/m/K; ThermalExpansionCoefficient=15.000000000000 µm/m/K; YieldStrength=345.000000000000 MPa; YoungsModulus=21.000000000000 GPa
  References = -> [board_solid]
FEATURE [Fem::ConstraintTemperature] ConstraintTemperature
  CFlux = 0
  ConstraintType = 1
  NormalDirection = (0,0,-1)
  Normals = (5) [(0,0,-1),(0,0,-1),(0,0,-1),(0,0,-1),(0,0,-1)]
  Points = (5) [(4.90232,-22.4091,-0.0711),(-0.151779,-11.3575,-0.0711),(4.90232,-11.3575,-0.0711),(9.95642,-11.3575,-0.0711),(4.90232,-0.3059,-0.0711)]
  References = -> [coppers_drilled]
  Temperature = 300
FEATURE [Fem::ConstraintTemperature] ConstraintTemperature001
  CFlux = 0
  ConstraintType = 1
  NormalDirection = (0,0,1)
  Normals = (9) [(0,0,1),(0,0,1),(0,0,1),(0,0,1),(0,0,1),(0,0,1),(0,0,1),(0,0,1),(0,0,1)]
  Points = (9) [(1.9,-18.22,0.84),(2.4,-18.22,0.84),(2.9,-18.22,0.84),(1.9,-17.72,0.84),(2.4,-17.72,0.84),(2.9,-17.72,0.84),(1.9,-17.22,0.84),(2.4,-17.22,0.84),(2.9,-17.22,0.84)]
  References = -> [Box]
  Temperature = 400
FEATURE [App::TextDocument] SolverElmerOutput
  Text = <blob: 12732907 chars omitted>
FEATURE [Fem::FemPostPipeline] SolverElmerResult
  Mode = 2
FEATURE [Fem::FemSolverObjectPython] SolverElmer  # FEM object (typed FeaturePython)
  ElmerOutput = -> SolverElmerOutput
  ElmerResult = -> SolverElmerResult
  Group = -> [Heat]
  SteadyStateMaxIterations = 1
  SteadyStateMinIterations = 0
FEATURE [Fem::FemAnalysis] Analysis
  Group = -> [FEMMeshGmsh,SolverElmer,MaterialSolid,MaterialSolid001,ConstraintTemperature,ConstraintTemperature001,SolverElmerOutput,SolverElmerResult]
